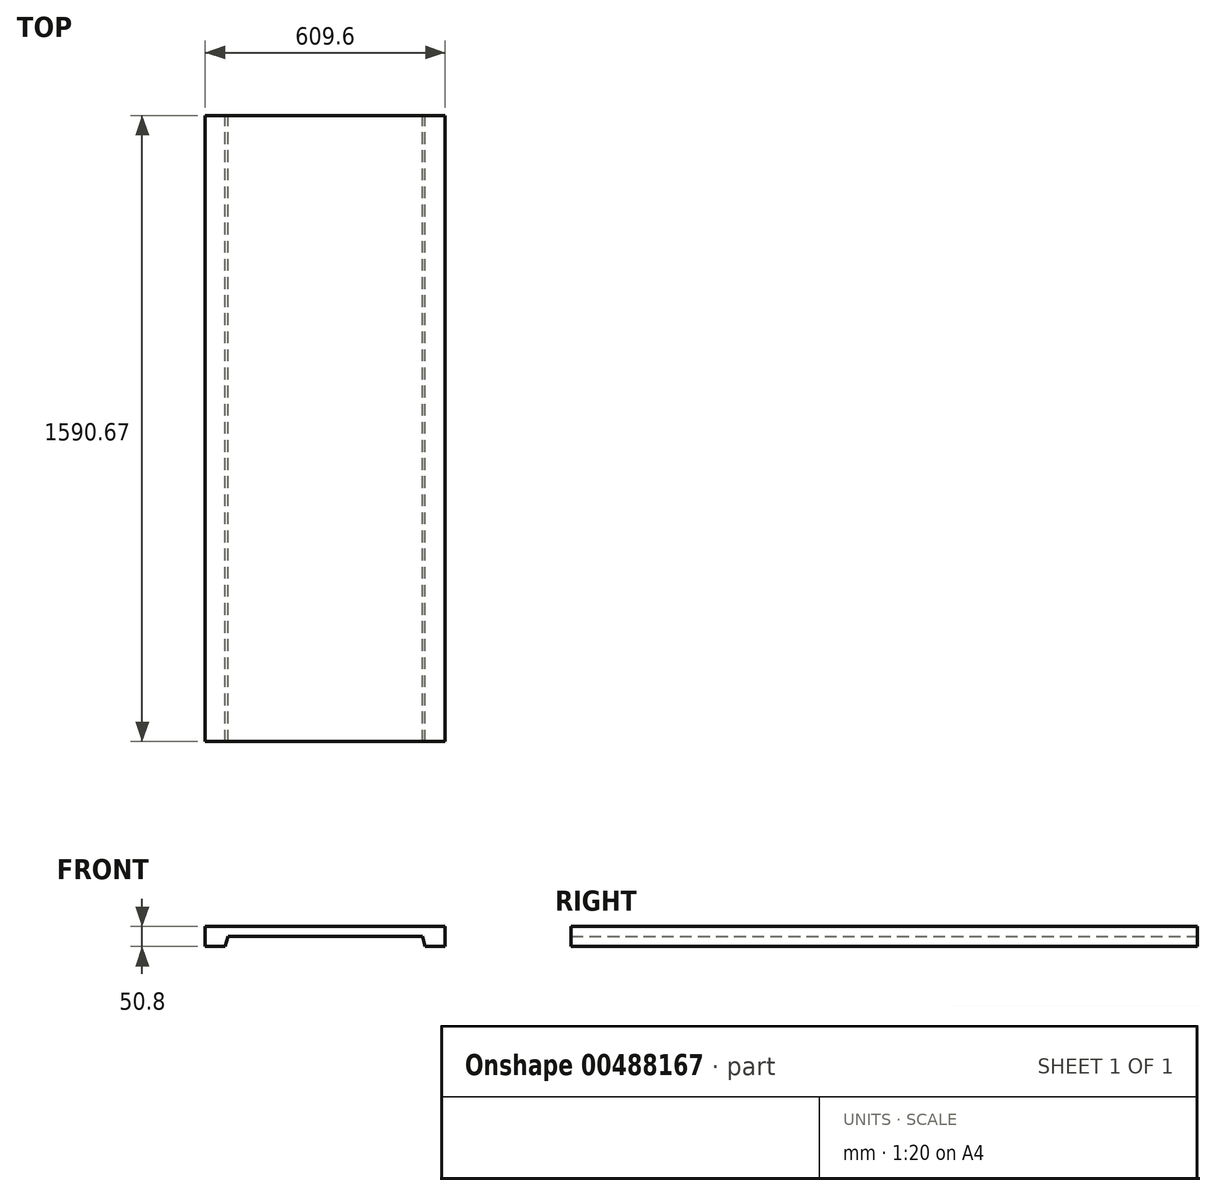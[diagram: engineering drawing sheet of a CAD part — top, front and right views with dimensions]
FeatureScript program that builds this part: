
annotation { "Feature Type Name" : "Feature", "Feature Type Description" : "" }
export const myFeature = defineFeature(function(context is Context, id is Id, definition is map)
    precondition{}
    {
        {
            var Q0;
            Q0=qCreatedBy(makeId("Front.planeOp"),FACE);
            var sketch = newSketch(context, id + "F0", { "sketchPlane" : qUnion([Q0])});
            skLineSegment(sketch, "E0", {"start": v(0, 0) * mm, "end": v(0, 50.8) * mm});
            skLineSegment(sketch, "E1", {"start": v(0, 50.8) * mm, "end": v(609.6, 50.8) * mm});
            skLineSegment(sketch, "E2", {"start": v(609.6, 50.8) * mm, "end": v(609.6, 0) * mm});
            skLineSegment(sketch, "E3", {"start": v(609.6, 0) * mm, "end": v(558.8, 0) * mm});
            skLineSegment(sketch, "E4", {"start": v(558.8, 0) * mm, "end": v(552, 25.4) * mm});
            skLineSegment(sketch, "E5", {"start": v(552, 25.4) * mm, "end": v(57.6, 25.4) * mm});
            skLineSegment(sketch, "E6", {"start": v(57.6, 25.4) * mm, "end": v(50.8, 0) * mm});
            skLineSegment(sketch, "E7", {"start": v(50.8, 0) * mm, "end": v(0, 0) * mm});
            skSolve(sketch);
        }
        {
            var Q0;
            Q0=makeQuery(id+"F0.imprint","IMPRINT",FACE,{"disambiguationData":[TD([[makeQuery(id+"F0.imprint","IMPRINT",EDGE,{"derivedFrom":sQuery(id+"F0.wireOp",EDGE,"E0")}),-1.0]])]});
            extrude(context, id + "F1", {"entities" : qUnion([Q0]), "depth" : 1590.67 * mm, "offsetDistance" : 25.4 * mm});
        }
    });
